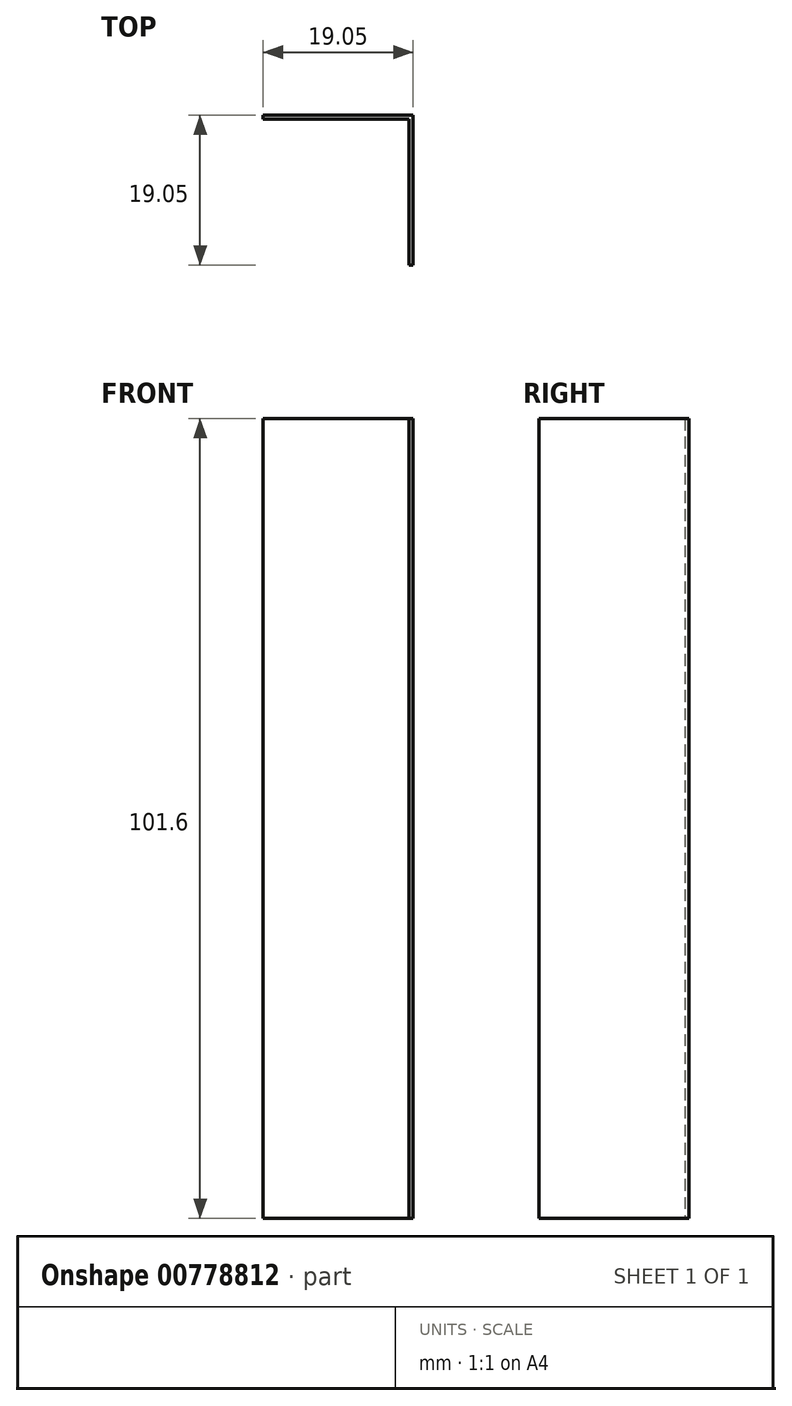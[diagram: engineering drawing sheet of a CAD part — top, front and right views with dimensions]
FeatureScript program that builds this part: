
annotation { "Feature Type Name" : "Feature", "Feature Type Description" : "" }
export const myFeature = defineFeature(function(context is Context, id is Id, definition is map)
    precondition{}
    {
        {
            var Q0;
            Q0=qCreatedBy(makeId("Top.planeOp"),FACE);
            var sketch = newSketch(context, id + "F0", { "sketchPlane" : qUnion([Q0])});
            skLineSegment(sketch, "E0", {"start": v(0, 0) * mm, "end": v(19.05, 0) * mm});
            skLineSegment(sketch, "E1", {"start": v(19.05, 0) * mm, "end": v(19.05, -19.05) * mm});
            skLineSegment(sketch, "E2", {"start": v(19.05, -19.05) * mm, "end": v(18.54, -19.05) * mm});
            skLineSegment(sketch, "E3", {"start": v(18.54, -19.05) * mm, "end": v(18.54, -0.5) * mm});
            skLineSegment(sketch, "E4", {"start": v(18.54, -0.5) * mm, "end": v(0, -0.5) * mm});
            skLineSegment(sketch, "E5", {"start": v(0, -0.5) * mm, "end": v(0, 0) * mm});
            skSolve(sketch);
        }
        {
            var Q0;
            Q0=makeQuery(id+"F0.imprint","IMPRINT",FACE,{"disambiguationData":[TD([[makeQuery(id+"F0.imprint","IMPRINT",EDGE,{"derivedFrom":sQuery(id+"F0.wireOp",EDGE,"E0")}),-1.0]])]});
            extrude(context, id + "F1", {"entities" : qUnion([Q0]), "depth" : 101.6 * mm, "offsetDistance" : 25.4 * mm});
        }
    });
